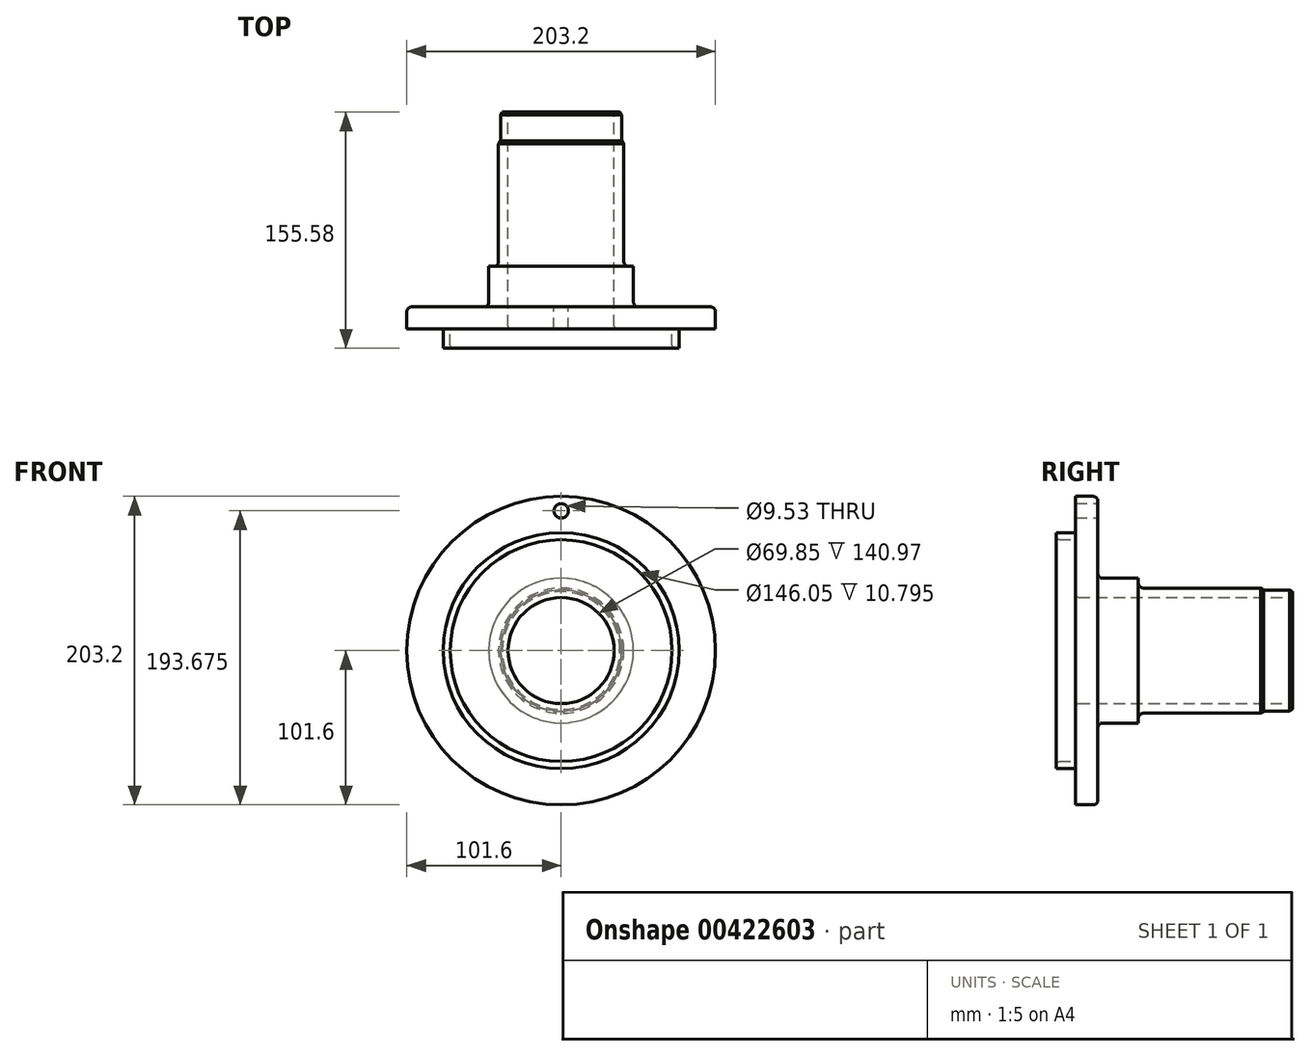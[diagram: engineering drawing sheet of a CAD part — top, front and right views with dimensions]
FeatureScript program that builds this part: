
annotation { "Feature Type Name" : "Feature", "Feature Type Description" : "" }
export const myFeature = defineFeature(function(context is Context, id is Id, definition is map)
    precondition{}
    {
        {
            var Q0;
            Q0=qCreatedBy(makeId("Right.planeOp"),FACE);
            var sketch = newSketch(context, id + "F0", { "sketchPlane" : qUnion([Q0])});
            skLineSegment(sketch, "E0", {"start": v(-165.17, 0) * mm, "end": v(164.08, 0) * mm, "construction": true});
            skLineSegment(sketch, "E1", {"start": v(-165.17, 101.6) * mm, "end": v(-165.17, 0) * mm});
            skLineSegment(sketch, "E2", {"start": v(-165.17, 101.6) * mm, "end": v(-150.56, 101.6) * mm});
            skLineSegment(sketch, "E3", {"start": v(-150.56, 101.6) * mm, "end": v(-150.56, 47.65) * mm});
            skLineSegment(sketch, "E4", {"start": v(-150.56, 47.65) * mm, "end": v(-123.9, 47.65) * mm});
            skLineSegment(sketch, "E5", {"start": v(-123.9, 47.65) * mm, "end": v(-123.9, 41.26) * mm});
            skLineSegment(sketch, "E6", {"start": v(-123.9, 41.26) * mm, "end": v(-41.34, 41.26) * mm});
            skLineSegment(sketch, "E7", {"start": v(-41.34, 41.26) * mm, "end": v(-41.34, 39.84) * mm});
            skLineSegment(sketch, "E8", {"start": v(-41.34, 39.84) * mm, "end": v(-22.3, 39.84) * mm});
            skLineSegment(sketch, "E9", {"start": v(-22.3, 39.84) * mm, "end": v(-22.3, 0) * mm});
            skLineSegment(sketch, "E10", {"start": v(-165.17, 0) * mm, "end": v(-22.3, 0) * mm});
            skSolve(sketch);
        }
        {
            var Q0;
            Q0=makeQuery(id+"F0.imprint","IMPRINT",FACE,{"disambiguationData":[TD([[makeQuery(id+"F0.imprint","IMPRINT",EDGE,{"derivedFrom":sQuery(id+"F0.wireOp",EDGE,"E1")}),1.0]])]});
            var Q1;
            Q1=sQuery(id+"F0.wireOp",EDGE,"E0");
            revolve(context, id + "F1", {"entities" : qUnion([Q0]), "axis" : qUnion([Q1]), "revolveType" : RevolveType.FULL});
        }
        {
            var Q0;
            Q0=makeQuery(id+"F1.opRevolve","SWEPT_FACE",FACE,{"disambiguationData":[OSD([sQuery(id+"F0.wireOp",EDGE,"E3")])]});
            var sketch = newSketch(context, id + "F2", { "sketchPlane" : qUnion([Q0])});
            skCircle(sketch, "E11", {"center": v(0, 0) * mm, "radius": 92.08 * mm, "construction": true});
            skCircle(sketch, "E12", {"center": v(0, 92.08) * mm, "radius": 4.76 * mm});
            skSolve(sketch);
        }
        {
            var Q0;
            Q0 = qSketchRegion(id + "F2", true);
            extrude(context, id + "F3", {"entities" : qUnion([Q0]), "operationType" : NewBodyOperationType.REMOVE, "oppositeDirection" : true, "depth" : 25.4 * mm});
        }
        {
            var Q0;
            Q0=makeQuery(id+"F1.opRevolve","SWEPT_FACE",FACE,{"disambiguationData":[OSD([sQuery(id+"F0.wireOp",EDGE,"E9")])]});
            var sketch = newSketch(context, id + "F4", { "sketchPlane" : qUnion([Q0])});
            skCircle(sketch, "E13", {"center": v(0, 0) * mm, "radius": 34.93 * mm});
            skSolve(sketch);
        }
        {
            var Q0;
            Q0 = qSketchRegion(id + "F4", true);
            extrude(context, id + "F5", {"entities" : qUnion([Q0]), "operationType" : NewBodyOperationType.REMOVE, "oppositeDirection" : true, "depth" : 152.4 * mm});
        }
        {
            var Q0;
            Q0=makeQuery(id+"F1.opRevolve","SWEPT_EDGE",EDGE,{"disambiguationData":[OSD([sQuery(id+"F0.wireOp",EDGE,"E8"),sQuery(id+"F0.wireOp",EDGE,"E9")])]});
            chamfer(context, id + "F6", {"entities" : qUnion([Q0]), "chamferType" : ChamferType.OFFSET_ANGLE, "width" : 1.9 * mm, "oppositeDirection" : false, "angle" : 30 * degree, "tangentPropagation" : true});
        }
        {
            var Q0;
            Q0=makeQuery(id+"F1.opRevolve","SWEPT_EDGE",EDGE,{"disambiguationData":[OSD([sQuery(id+"F0.wireOp",EDGE,"E6"),sQuery(id+"F0.wireOp",EDGE,"E7")])]});
            chamfer(context, id + "F7", {"entities" : qUnion([Q0]), "chamferType" : ChamferType.OFFSET_ANGLE, "width" : 1.9 * mm, "oppositeDirection" : false, "angle" : 30 * degree, "tangentPropagation" : true});
        }
        {
            var Q0;
            Q0=makeQuery(id+"F1.opRevolve","SWEPT_EDGE",EDGE,{"disambiguationData":[OSD([sQuery(id+"F0.wireOp",EDGE,"E5"),sQuery(id+"F0.wireOp",EDGE,"E6")])]});
            var Q1;
            Q1=makeQuery(id+"F1.opRevolve","SWEPT_EDGE",EDGE,{"disambiguationData":[OSD([sQuery(id+"F0.wireOp",EDGE,"E3"),sQuery(id+"F0.wireOp",EDGE,"E4")])]});
            var Q2;
            Q2=makeQuery(id+"F1.opRevolve","SWEPT_EDGE",EDGE,{"disambiguationData":[OSD([sQuery(id+"F0.wireOp",EDGE,"E2"),sQuery(id+"F0.wireOp",EDGE,"E3")])]});
            fillet(context, id + "F8", {"entities" : qUnion([Q0, Q1, Q2]), "radius" : 3.17 * mm, "tangentPropagation" : true, "allowEdgeOverflow" : false});
        }
        {
            var Q0;
            Q0=makeQuery(id+"F1.opRevolve","SWEPT_FACE",FACE,{"disambiguationData":[OSD([sQuery(id+"F0.wireOp",EDGE,"E1")])]});
            var sketch = newSketch(context, id + "F9", { "sketchPlane" : qUnion([Q0])});
            skCircle(sketch, "E14", {"center": v(0, 0) * mm, "radius": 77.7 * mm});
            skCircle(sketch, "E15", {"center": v(0, 0) * mm, "radius": 73.03 * mm});
            skSolve(sketch);
        }
        {
            var Q0;
            Q0 = qSketchRegion(id + "F9", true);
            extrude(context, id + "F10", {"entities" : qUnion([Q0]), "operationType" : NewBodyOperationType.ADD, "depth" : 12.7 * mm});
        }
        {
            var Q0;
            Q0=makeQuery(id+"F10.opExtrude","CAP_EDGE",EDGE,{"disambiguationData":[OSD([sQuery(id+"F9.wireOp",EDGE,"E15")])],"isStart":false});
            var Q1;
            Q1=makeQuery(id+"F5.boolean.opBoolean","INTERSECT",EDGE,{"derivedFrom":[makeQuery(id+"F1.opRevolve","SWEPT_FACE",FACE,{"disambiguationData":[OSD([sQuery(id+"F0.wireOp",EDGE,"E1")])]}),makeQuery(id+"F5.opExtrude","SWEPT_FACE",FACE,{"disambiguationData":[OSD([sQuery(id+"F4.wireOp",EDGE,"E13")])]})]});
            fillet(context, id + "F11", {"entities" : qUnion([Q0, Q1]), "radius" : 1.9 * mm, "tangentPropagation" : true, "allowEdgeOverflow" : false});
        }
    });
